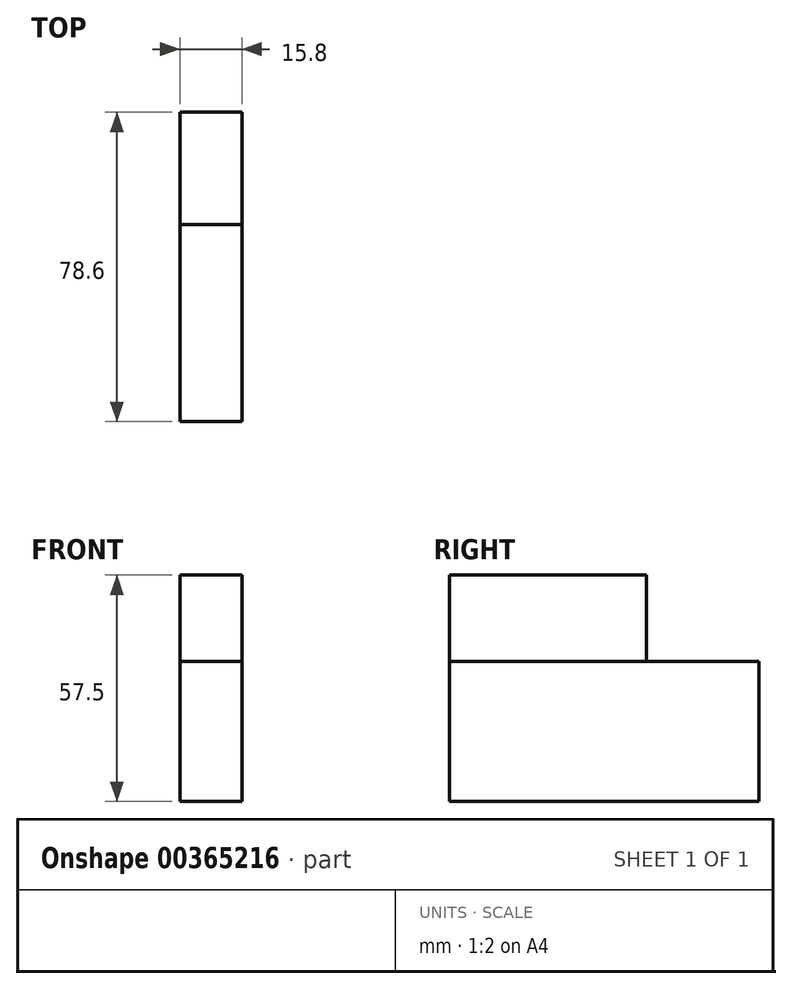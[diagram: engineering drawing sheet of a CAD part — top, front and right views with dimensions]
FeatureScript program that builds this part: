
annotation { "Feature Type Name" : "Feature", "Feature Type Description" : "" }
export const myFeature = defineFeature(function(context is Context, id is Id, definition is map)
    precondition{}
    {
        {
            var Q0;
            Q0=qCreatedBy(makeId("Top.planeOp"),FACE);
            var sketch = newSketch(context, id + "F0", { "sketchPlane" : qUnion([Q0])});
            skLineSegment(sketch, "E0.bottom", {"start": v(7.9, -39.3) * mm, "end": v(-7.9, -39.3) * mm});
            skLineSegment(sketch, "E0.top", {"start": v(7.9, 39.3) * mm, "end": v(-7.9, 39.3) * mm});
            skLineSegment(sketch, "E0.left", {"start": v(7.9, -39.3) * mm, "end": v(7.9, 39.3) * mm});
            skLineSegment(sketch, "E0.right", {"start": v(-7.9, -39.3) * mm, "end": v(-7.9, 39.3) * mm});
            skPoint(sketch, "E0.middle", {"position": v(0, 0) * mm});
            skSolve(sketch);
        }
        {
            var Q0;
            Q0 = qSketchRegion(id + "F0", true);
            extrude(context, id + "F1", {"entities" : qUnion([Q0]), "depth" : 35.5 * mm});
        }
        {
            var Q0;
            Q0=makeQuery(id+"F1.opExtrude","CAP_FACE",FACE,{"disambiguationData":[OSD([sQuery(id+"F0.wireOp",EDGE,"E0.bottom"),sQuery(id+"F0.wireOp",EDGE,"E0.top"),sQuery(id+"F0.wireOp",EDGE,"E0.left"),sQuery(id+"F0.wireOp",EDGE,"E0.right")])],"isStart":false});
            var sketch = newSketch(context, id + "F2", { "sketchPlane" : qUnion([Q0])});
            skLineSegment(sketch, "E1.bottom", {"start": v(-7.9, -39.3) * mm, "end": v(7.9, -39.3) * mm});
            skLineSegment(sketch, "E1.top", {"start": v(-7.9, 10.7) * mm, "end": v(7.9, 10.7) * mm});
            skLineSegment(sketch, "E1.left", {"start": v(-7.9, -39.3) * mm, "end": v(-7.9, 10.7) * mm});
            skLineSegment(sketch, "E1.right", {"start": v(7.9, -39.3) * mm, "end": v(7.9, 10.7) * mm});
            skSolve(sketch);
        }
        {
            var Q0;
            Q0 = qSketchRegion(id + "F2", true);
            extrude(context, id + "F3", {"entities" : qUnion([Q0]), "depth" : 22 * mm});
        }
    });
